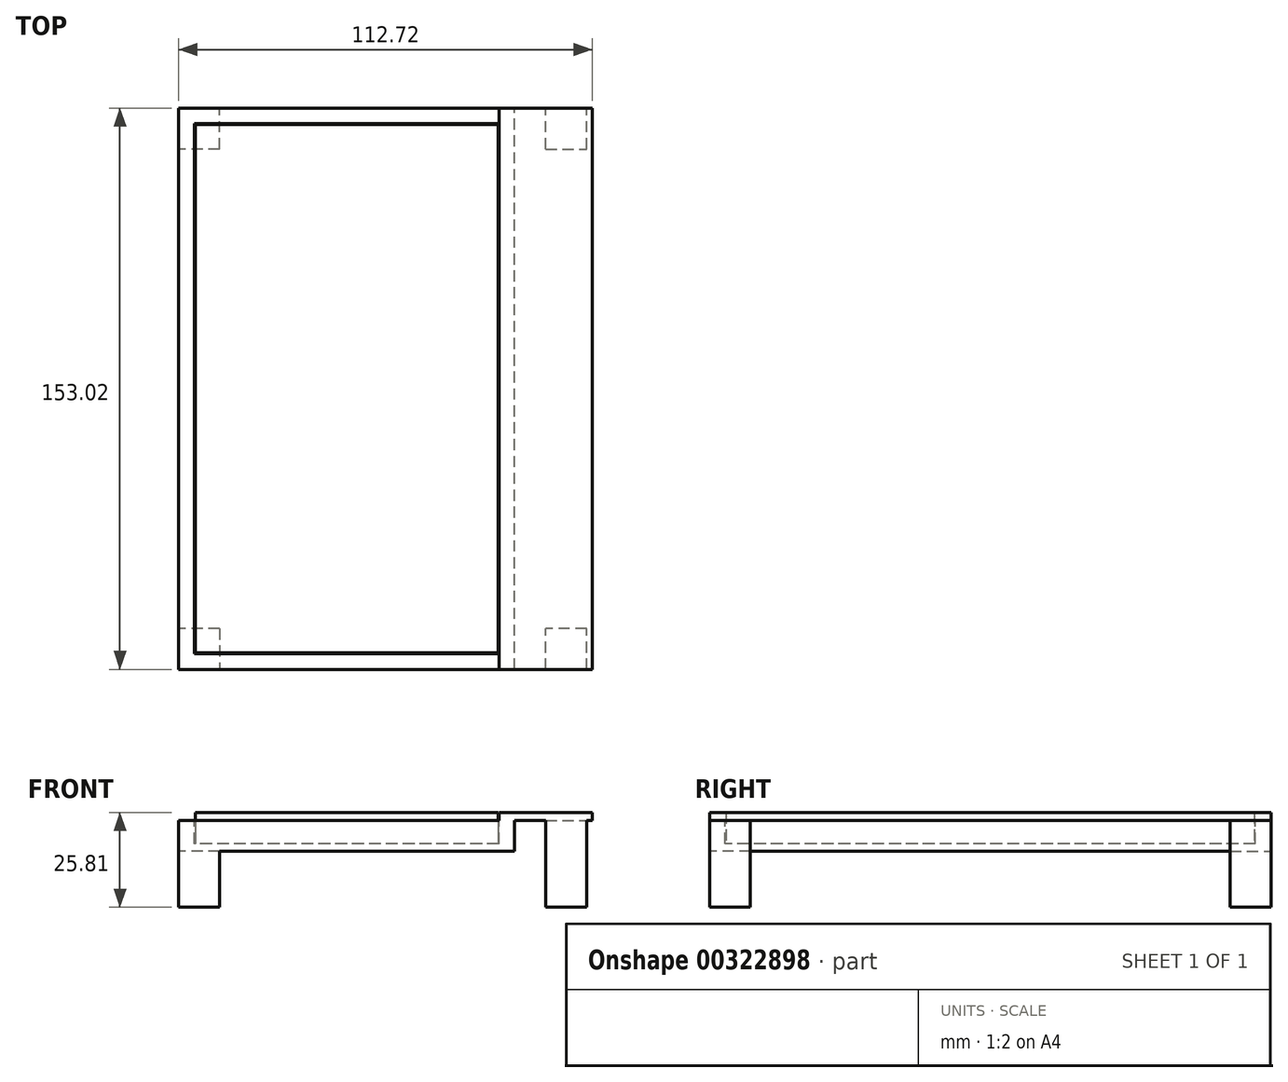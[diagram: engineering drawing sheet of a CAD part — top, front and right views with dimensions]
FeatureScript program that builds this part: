
annotation { "Feature Type Name" : "Feature", "Feature Type Description" : "" }
export const myFeature = defineFeature(function(context is Context, id is Id, definition is map)
    precondition{}
    {
        {
            var Q0;
            Q0=qCreatedBy(makeId("Top.planeOp"),FACE);
            var sketch = newSketch(context, id + "F0", { "sketchPlane" : qUnion([Q0])});
            skLineSegment(sketch, "E0.top", {"start": v(41.28, -72) * mm, "end": v(-41.27, -72) * mm});
            skLineSegment(sketch, "E0.left", {"start": v(41.28, 72) * mm, "end": v(41.28, -72) * mm});
            skLineSegment(sketch, "E0.right", {"start": v(-41.27, 72) * mm, "end": v(-41.27, -72) * mm});
            skLineSegment(sketch, "E1", {"start": v(41.28, 72) * mm, "end": v(-41.27, 72) * mm});
            skSolve(sketch);
        }
        {
            var Q0;
            Q0 = qSketchRegion(id + "F0", true);
            extrude(context, id + "F1", {"entities" : qUnion([Q0]), "depth" : 8.46 * mm});
        }
        {
            var Q0;
            Q0=makeQuery(id+"F1.opExtrude","CAP_FACE",FACE,{"disambiguationData":[OSD([sQuery(id+"F0.wireOp",EDGE,"E0.top"),sQuery(id+"F0.wireOp",EDGE,"E0.left"),sQuery(id+"F0.wireOp",EDGE,"E0.right"),sQuery(id+"F0.wireOp",EDGE,"E1")])],"isStart":false});
            var sketch = newSketch(context, id + "F2", { "sketchPlane" : qUnion([Q0])});
            skLineSegment(sketch, "E2.0", {"start": v(41.54, 72.27) * mm, "end": v(-41.54, 72.27) * mm});
            skLineSegment(sketch, "E2.1", {"start": v(41.54, 72.27) * mm, "end": v(41.54, -72.27) * mm});
            skLineSegment(sketch, "E2.2", {"start": v(41.54, -72.27) * mm, "end": v(-41.54, -72.27) * mm});
            skLineSegment(sketch, "E2.3", {"start": v(-41.54, 72.27) * mm, "end": v(-41.54, -72.27) * mm});
            skLineSegment(sketch, "E3.0", {"start": v(45.78, 76.51) * mm, "end": v(-45.78, 76.51) * mm});
            skLineSegment(sketch, "E3.1", {"start": v(45.78, 76.51) * mm, "end": v(45.78, -76.51) * mm});
            skLineSegment(sketch, "E3.2", {"start": v(45.78, -76.51) * mm, "end": v(-45.78, -76.51) * mm});
            skLineSegment(sketch, "E3.3", {"start": v(-45.78, 76.51) * mm, "end": v(-45.78, -76.51) * mm});
            skSolve(sketch);
        }
        {
            var Q0;
            Q0 = qSketchRegion(id + "F2", true);
            extrude(context, id + "F3", {"entities" : qUnion([Q0]), "oppositeDirection" : true, "depth" : 8.46 * mm, "hasSecondDirection" : true, "secondDirectionOppositeDirection" : true, "secondDirectionDepth" : 2.1 * mm});
        }
        {
            var Q0;
            Q0=makeQuery(id+"F3.opExtrude","SWEPT_FACE",FACE,{"disambiguationData":[OSD([sQuery(id+"F2.wireOp",EDGE,"E3.0")])]});
            var sketch = newSketch(context, id + "F4", { "sketchPlane" : qUnion([Q0])});
            skLineSegment(sketch, "E4.bottom", {"start": v(-45.78, 0) * mm, "end": v(45.78, 0) * mm});
            skLineSegment(sketch, "E4.top", {"start": v(-45.78, -2.1) * mm, "end": v(45.78, -2.1) * mm});
            skLineSegment(sketch, "E4.left", {"start": v(-45.78, 0) * mm, "end": v(-45.78, -2.1) * mm});
            skLineSegment(sketch, "E4.right", {"start": v(45.78, 0) * mm, "end": v(45.78, -2.1) * mm});
            skSolve(sketch);
        }
        {
            var Q0;
            Q0 = qSketchRegion(id + "F4", true);
            var Q1;
            Q1=makeQuery(id+"F3.opExtrude","SWEPT_FACE",FACE,{"disambiguationData":[OSD([sQuery(id+"F2.wireOp",EDGE,"E3.2")])]});
            extrude(context, id + "F5", {"entities" : qUnion([Q0]), "operationType" : NewBodyOperationType.ADD, "endBound" : BoundingType.UP_TO_SURFACE, "oppositeDirection" : true, "endBoundEntityFace" : qUnion([Q1]), "depth" : 25.4 * mm});
        }
        {
            var Q0;
            Q0=makeQuery(id+"F3.opExtrude","CAP_FACE",FACE,{"disambiguationData":[OSD([sQuery(id+"F2.wireOp",EDGE,"E2.0"),sQuery(id+"F2.wireOp",EDGE,"E2.1"),sQuery(id+"F2.wireOp",EDGE,"E2.2"),sQuery(id+"F2.wireOp",EDGE,"E2.3"),sQuery(id+"F2.wireOp",EDGE,"E3.0"),sQuery(id+"F2.wireOp",EDGE,"E3.1"),sQuery(id+"F2.wireOp",EDGE,"E3.2"),sQuery(id+"F2.wireOp",EDGE,"E3.3")])],"isStart":true});
            var sketch = newSketch(context, id + "F6", { "sketchPlane" : qUnion([Q0])});
            skLineSegment(sketch, "E5.bottom", {"start": v(41.54, -76.51) * mm, "end": v(66.94, -76.51) * mm});
            skLineSegment(sketch, "E5.top", {"start": v(41.54, 76.51) * mm, "end": v(66.94, 76.51) * mm});
            skLineSegment(sketch, "E5.left", {"start": v(41.54, -76.51) * mm, "end": v(41.54, 76.51) * mm});
            skLineSegment(sketch, "E5.right", {"start": v(66.94, -76.51) * mm, "end": v(66.94, 76.51) * mm});
            skSolve(sketch);
        }
        {
            var Q0;
            Q0 = qSketchRegion(id + "F6", true);
            extrude(context, id + "F7", {"entities" : qUnion([Q0]), "operationType" : NewBodyOperationType.ADD, "depth" : 2.1 * mm});
        }
        {
            var Q0;
            Q0=makeQuery(id+"F5.opExtrude","SWEPT_FACE",FACE,{"disambiguationData":[OSD([sQuery(id+"F4.wireOp",EDGE,"E4.top")])]});
            var sketch = newSketch(context, id + "F8", { "sketchPlane" : qUnion([Q0])});
            skLineSegment(sketch, "E6.bottom", {"start": v(-45.78, -76.51) * mm, "end": v(-34.65, -76.51) * mm});
            skLineSegment(sketch, "E6.top", {"start": v(-45.78, -65.38) * mm, "end": v(-34.65, -65.38) * mm});
            skLineSegment(sketch, "E6.left", {"start": v(-45.78, -76.51) * mm, "end": v(-45.78, -65.38) * mm});
            skLineSegment(sketch, "E6.right", {"start": v(-34.65, -76.51) * mm, "end": v(-34.65, -65.38) * mm});
            skLineSegment(sketch, "E7.bottom", {"start": v(-45.78, 76.51) * mm, "end": v(-34.65, 76.51) * mm});
            skLineSegment(sketch, "E7.top", {"start": v(-45.78, 65.38) * mm, "end": v(-34.65, 65.38) * mm});
            skLineSegment(sketch, "E7.left", {"start": v(-45.78, 76.51) * mm, "end": v(-45.78, 65.38) * mm});
            skLineSegment(sketch, "E7.right", {"start": v(-34.65, 76.51) * mm, "end": v(-34.65, 65.38) * mm});
            skLineSegment(sketch, "E8.bottom", {"start": v(54.25, 65.38) * mm, "end": v(65.38, 65.38) * mm});
            skLineSegment(sketch, "E8.top", {"start": v(54.25, 76.51) * mm, "end": v(65.38, 76.51) * mm});
            skLineSegment(sketch, "E8.left", {"start": v(54.25, 65.38) * mm, "end": v(54.25, 76.51) * mm});
            skLineSegment(sketch, "E8.right", {"start": v(65.38, 65.38) * mm, "end": v(65.38, 76.51) * mm});
            skLineSegment(sketch, "E9.bottom", {"start": v(65.38, -76.51) * mm, "end": v(54.25, -76.51) * mm});
            skLineSegment(sketch, "E9.top", {"start": v(65.38, -65.38) * mm, "end": v(54.25, -65.38) * mm});
            skLineSegment(sketch, "E9.left", {"start": v(65.38, -76.51) * mm, "end": v(65.38, -65.38) * mm});
            skLineSegment(sketch, "E9.right", {"start": v(54.25, -76.51) * mm, "end": v(54.25, -65.38) * mm});
            skSolve(sketch);
        }
        {
            var Q0;
            Q0 = qSketchRegion(id + "F8", true);
            extrude(context, id + "F9", {"entities" : qUnion([Q0]), "operationType" : NewBodyOperationType.ADD, "depth" : 15.24 * mm, "hasSecondDirection" : true, "secondDirectionBound" : SecondDirectionBoundingType.UP_TO_NEXT, "secondDirectionOppositeDirection" : true, "secondDirectionDepth" : 25.4 * mm});
        }
    });
